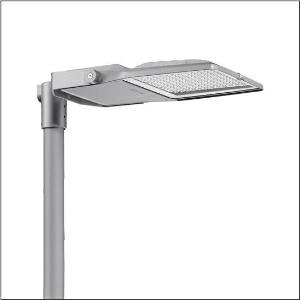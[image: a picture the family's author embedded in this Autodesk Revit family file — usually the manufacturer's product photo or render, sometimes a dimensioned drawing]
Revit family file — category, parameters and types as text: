
# Revit family: floodlight_fl_21_iq_midi___pl33t_5xa7781f4f3a_8e83
name_source: partatom
category: Lighting Fixtures
units: mm (PartAtom-declared; Revit-internal decimal feet)

## family parameters
Cut with Voids When Loaded = No
Host = Face
Light Source = No
Part Type = Normal
Room Calculation Point = No
Round Connector Dimension = Use Diameter
Shared = No

## types (1)
- --- (1 x LED, 36900 lm, 270.2 W, 4000K)
    Apparent Load = 270 VA
    CIE Flux Codes = 26 75 99 100 100
    Color Rendering = 70
    Color Temperature = 4000K
    Default Elevation = 1800 mm
    Description = Floodlight FL 21 iQ midi, floodlight, primary light control with lens, of PMMA, primary optical cover: protective disc, of toughened safety glass, transparent, light distribution: PL33T, light emission: direct distribution, installation type: surface-mounted, lamps: LED, High Power LED, rated values: 36.900lm | 270,2W | 136,6lm/W (begin service life); end service life: 36.900lm | 286,6W; at 50% lumin. flux: 18.450lm | 117,7W | 156,8lm/W, colour temperature: 4000K, colour rendering: CRI > 70, light colour: 740, light setting 1 begin service life: 100% | 36.900lm | 270,2W | 136,6lm/W | 4.000K, light setting 1 end service life: 286,6W, further light settings possible, control: optimised constant luminous flux control (CLO 2.0), Desk-Remote (wireless, voltage-free reading and setting of iQ features in the workshop via application-optimized NFC function/RFID function), Light-Fading, Smart-Wire, Night-Set, Lumen-Switch, Temp-Guard, Auto-Match, pre-setting: linear dimming characteristic, with terminal, 6-pole, mains connection: 220..240V, AC, 50/60Hz, luminaire housing, of diecast aluminium, powder-coated, SITECO metallic grey (DB 702S), corrosivity category C5 mid according to DIN EN ISO 12944suitable for swimming poolschlorine-resistant, sealing non-destructively replaceable, please order mast flange separately, mast bracket, of steel, galvanised, powder-coated, SITECO metallic grey (DB 702S), protection rating (complete): IP66, insulation class (complete): insulation class II (safety insulation), certification: CE, ENEC, VDE, protection symbol: D, impact resistance: IK08, permissible operating ambient temperature: -40..+40°C, permissible operating ambient temperature for outdoor applications: -40..+50°C, standard: DIN EN 12944, LABS conformity tested according to VDMA 24364:2018-05, packaging unit: 1 piece

Light Distribution: PL33T
    Height = 76 mm
    Lamp = 1 x LED
    Lamp Light Flux = 36900 lm
    Lamp Power = 270.2 W
    Lamp count = 1
    Length = 657 mm
    Luminous efficacy = 137 lm/W
    Manufacturer = Siteco
    ModVariant = No
    Model = 5XA7781F4F3A
    Mounting Place = Pole
    Mounting Type = Pole annexe
    Number of Poles = 1
    OnlyDefault = Yes
    Power Factor = 1
    Product Name = Floodlight FL 21 iQ midi | PL33T
    Product group = floodlight | pylon annexe
    ProductGroupID = 6201
    Protection Class = Protection class II
    Protection Degree = IP 66
    RLX_Detail_Level = 1
    RLX_Emergency_Light_Flux = 0 lm
    RLX_Emergency_Type = 0
    RLX_Emergency_Type_DB = No
    RlxData = <blob elided: 153577 chars, md5=630a92a1>
    Socket = socket
    Standby Power = 0 W
    System Light Flux = 36900 lm
    System Power = 270 W
    Type Comments = factory setting: luminous flux: 100 % | dim-lin: 254 | 620 mA
    Type Image = l_1007123.jpg
    URL = http://relux.com
    VarID = @adj_104989
    Voltage = 0 V
    Weight = 0.00 kg
    Width = 442 mm

## geometry (parser evidence)
native form markers: Blend x4, Sweep x12
no freeform markers — native parametric forms only
